# Revit family: 07 Fascia-WPH-Terminedge-Extruded
name_source: partatom
category: Profiles
revit_build: Autodesk Revit Architecture 2012 (Build: 20110916_2132(x64)
units: mm (PartAtom-declared; Revit-internal decimal feet)

## types (3) — shared parameters
0.032" AlUMINUM FASCIA COVER = No
0.040" AlUMINUM FASCIA COVER = No
0.050" AlUMINUM FASCIA COVER = No
0.063" AlUMINUM FASCIA COVER = No
24GA GALV.FASCIA COVER = Yes
ALUMINUM EXTRUDED BASE = Yes
Architectural Design Manual = http://www.wph.com
Assembly Code = B3010400
Description = Single Ply Fascia
Finish = Metal - Hickman - A01 - Statuary_Bronze
Finish Note = Actual metal color chips are available upon request and should be used for final color approval.
Florida Product Approval = FL7424
Manufacturer = W.P. HICKMAN
MasterFormat Number = 07 71 19
MasterFormat Title = Roof Specialties
OmniClass Number = 23-35 20 31 11 21
OmniClass Title = Roof Endings And Trims
Revision Date = 02/26/10
Series = Extruded_TerminEdge
Type Comments = Fascia
URL = http://www.wph.com

## per-type parameters (varying)
| type | Coverage "C" | Face Height "A" | Model |
| Face Height 3 3/4" | 2 1/2" | 3 3/4" | TEX-375 |
| Face Height 5 1/4" | 4" | 5 1/4" | TEX-525 |
| Face Height 6 3/4" | 5 1/2" | 6 3/4" | TEX-675 |

## geometry (parser evidence)
native form markers: Sweep x2
no freeform markers — native parametric forms only
